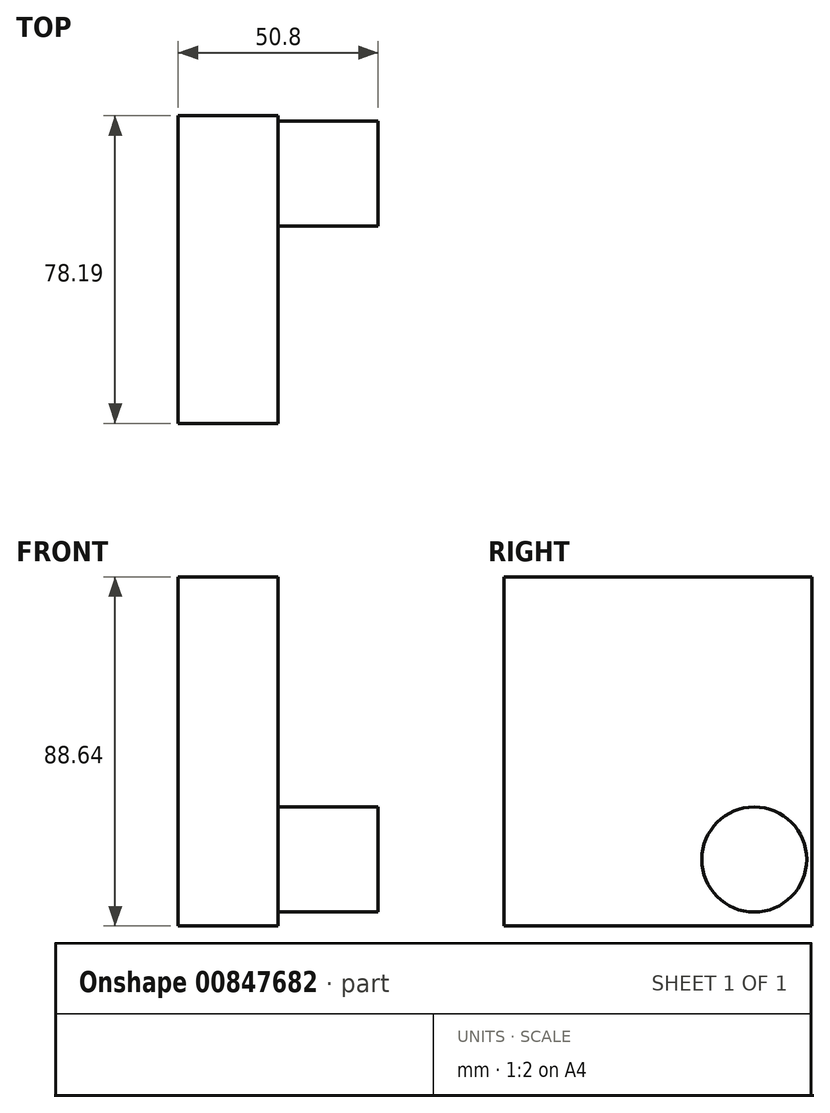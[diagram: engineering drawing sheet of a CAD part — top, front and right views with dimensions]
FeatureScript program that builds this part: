
annotation { "Feature Type Name" : "Feature", "Feature Type Description" : "" }
export const myFeature = defineFeature(function(context is Context, id is Id, definition is map)
    precondition{}
    {
        {
            var Q0;
            Q0=qCreatedBy(makeId("Right.planeOp"),FACE);
            var sketch = newSketch(context, id + "F0", { "sketchPlane" : qUnion([Q0])});
            skLineSegment(sketch, "E0.bottom", {"start": v(28.17, 0) * mm, "end": v(-50.02, 0) * mm});
            skLineSegment(sketch, "E0.top", {"start": v(28.17, 88.64) * mm, "end": v(-50.02, 88.64) * mm});
            skLineSegment(sketch, "E0.left", {"start": v(28.17, 0) * mm, "end": v(28.17, 88.64) * mm});
            skLineSegment(sketch, "E0.right", {"start": v(-50.02, 0) * mm, "end": v(-50.02, 88.64) * mm});
            skSolve(sketch);
        }
        {
            var Q0;
            Q0 = qSketchRegion(id + "F0", true);
            extrude(context, id + "F1", {"entities" : qUnion([Q0]), "depth" : 25.4 * mm, "offsetDistance" : 25.4 * mm});
        }
        {
            var Q0;
            Q0=makeQuery(id+"F1.opExtrude","CAP_FACE",FACE,{"disambiguationData":[OSD([sQuery(id+"F0.wireOp",EDGE,"E0.bottom"),sQuery(id+"F0.wireOp",EDGE,"E0.top"),sQuery(id+"F0.wireOp",EDGE,"E0.left"),sQuery(id+"F0.wireOp",EDGE,"E0.right")])],"isStart":false});
            var sketch = newSketch(context, id + "F2", { "sketchPlane" : qUnion([Q0])});
            skCircle(sketch, "E1", {"center": v(13.5, 16.84) * mm, "radius": 13.33 * mm});
            skSolve(sketch);
        }
        {
            var Q0;
            Q0 = qSketchRegion(id + "F2", true);
            extrude(context, id + "F3", {"entities" : qUnion([Q0]), "operationType" : NewBodyOperationType.ADD, "depth" : 25.4 * mm, "offsetDistance" : 25.4 * mm});
        }
    });
